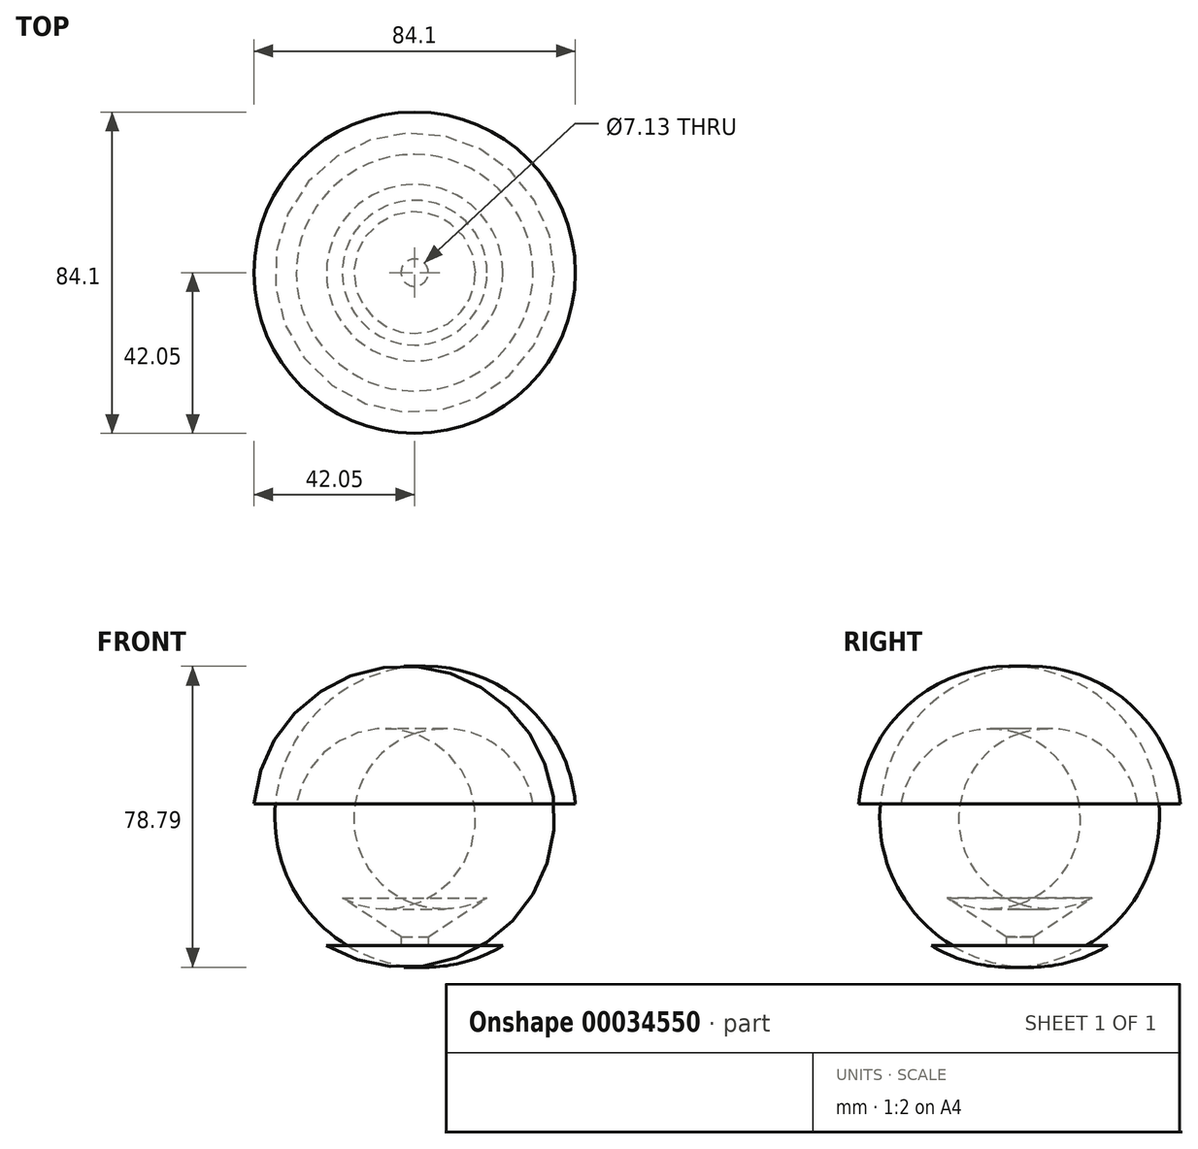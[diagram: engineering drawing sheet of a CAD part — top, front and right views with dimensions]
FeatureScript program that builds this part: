
annotation { "Feature Type Name" : "Feature", "Feature Type Description" : "" }
export const myFeature = defineFeature(function(context is Context, id is Id, definition is map)
    precondition{}
    {
        {
            var Q0;
            Q0=qCreatedBy(makeId("Front.planeOp"),FACE);
            var sketch = newSketch(context, id + "F0", { "sketchPlane" : qUnion([Q0])});
            skLineSegment(sketch, "E0", {"start": v(0, 0) * mm, "end": v(0, 12.48) * mm, "construction": true});
            skLineSegment(sketch, "E1", {"start": v(-30.97, 24.69) * mm, "end": v(-42.05, 24.69) * mm});
            skArc(sketch, "E2", {"start": v(-42.05, 24.69) * mm, "mid": v(-37.9, 3.38) * mm, "end": v(-23.09, -12.48) * mm});
            skArc(sketch, "E3", {"start": v(-30.97, 24.69) * mm, "mid": v(-28.92, 10.42) * mm, "end": v(-18.96, 0) * mm});
            skLineSegment(sketch, "E4", {"start": v(-23.09, -12.48) * mm, "end": v(-3.57, -12.48) * mm});
            skLineSegment(sketch, "E5", {"start": v(-3.57, -10.14) * mm, "end": v(-18.96, 0) * mm});
            skLineSegment(sketch, "E6", {"start": v(-3.57, -12.48) * mm, "end": v(-3.57, -10.14) * mm});
            skSolve(sketch);
        }
        {
            var Q0;
            Q0=makeQuery(id+"F0.imprint","IMPRINT",FACE,{"disambiguationData":[TD([[makeQuery(id+"F0.imprint","IMPRINT",EDGE,{"derivedFrom":sQuery(id+"F0.wireOp",EDGE,"E1")}),1.0]])]});
            var Q1;
            Q1=sQuery(id+"F0.wireOp",EDGE,"E0");
            revolve(context, id + "F1", {"entities" : qUnion([Q0]), "axis" : qUnion([Q1]), "revolveType" : RevolveType.FULL});
        }
    });
